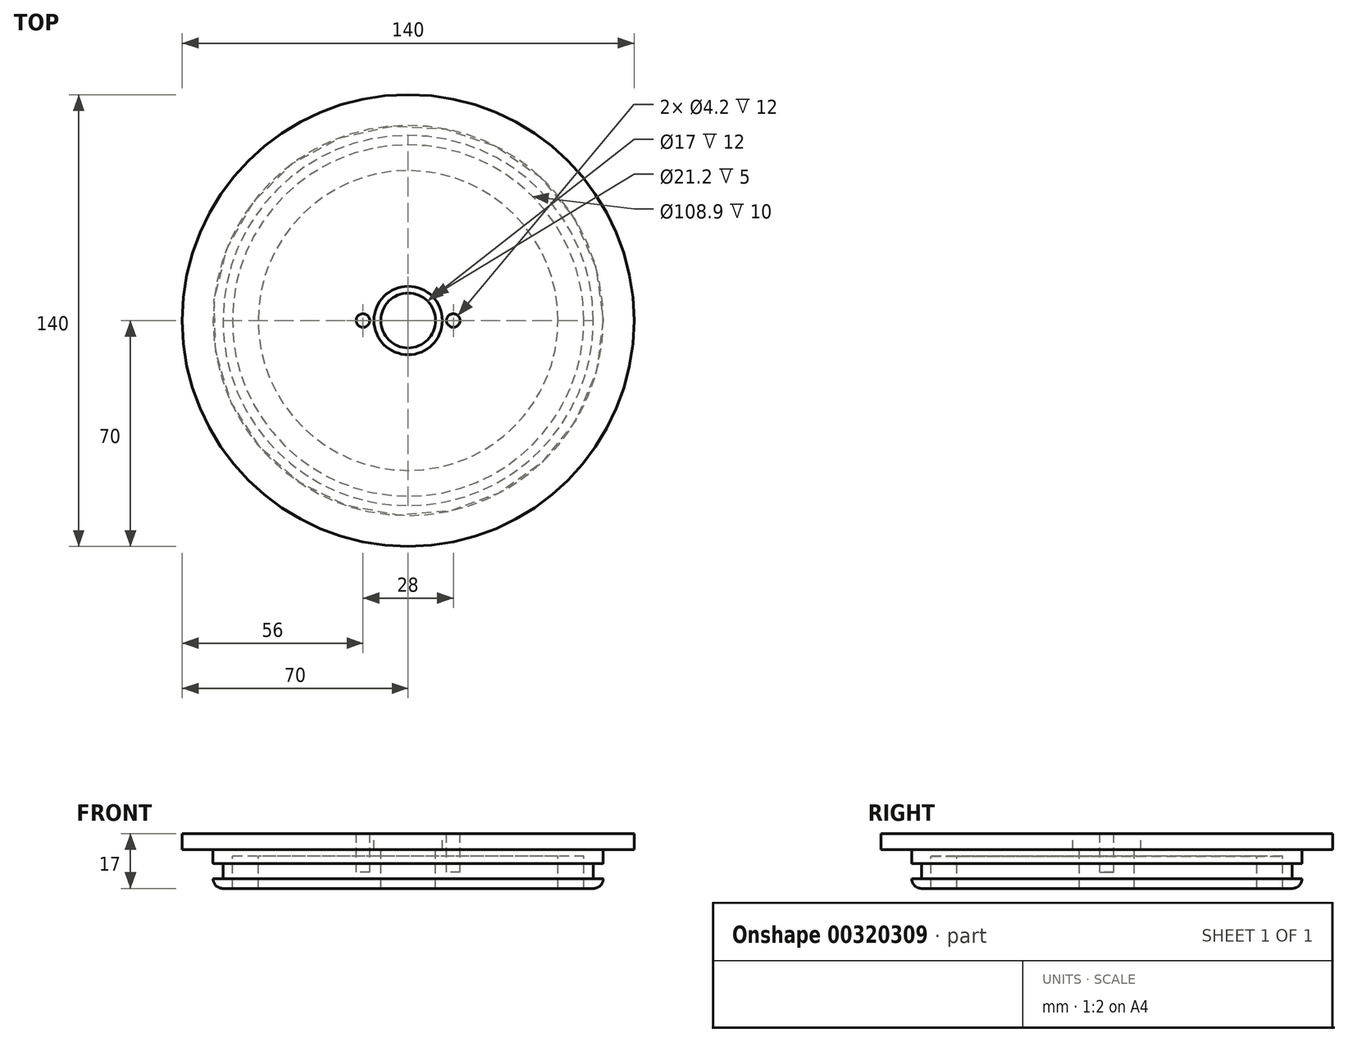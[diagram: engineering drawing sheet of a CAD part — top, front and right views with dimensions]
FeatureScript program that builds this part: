
annotation { "Feature Type Name" : "Feature", "Feature Type Description" : "" }
export const myFeature = defineFeature(function(context is Context, id is Id, definition is map)
    precondition{}
    {
        {
            var Q0;
            Q0=qCreatedBy(makeId("Front.planeOp"),FACE);
            var sketch = newSketch(context, id + "F0", { "sketchPlane" : qUnion([Q0])});
            skLineSegment(sketch, "E0", {"start": v(-10.6, 0) * mm, "end": v(-70, 0) * mm});
            skLineSegment(sketch, "E1", {"start": v(-70, 0) * mm, "end": v(-70, -5) * mm});
            skLineSegment(sketch, "E2", {"start": v(-70, -5) * mm, "end": v(-60.45, -5) * mm});
            skLineSegment(sketch, "E3", {"start": v(-60.45, -5) * mm, "end": v(-60.45, -9.15) * mm});
            skLineSegment(sketch, "E4", {"start": v(0, -17) * mm, "end": v(0, -5) * mm});
            skLineSegment(sketch, "E5", {"start": v(0, -17) * mm, "end": v(0, -14) * mm});
            skLineSegment(sketch, "E6", {"start": v(-57.38, -14) * mm, "end": v(-57.45, -14) * mm});
            skLineSegment(sketch, "E7", {"start": v(-57.38, -13.5) * mm, "end": v(-57.38, -9.8) * mm});
            skLineSegment(sketch, "E8", {"start": v(-57.88, -9.3) * mm, "end": v(-60.3, -9.3) * mm});
            skLineSegment(sketch, "E9", {"start": v(-57.88, -14) * mm, "end": v(-60.3, -14) * mm});
            skPoint(sketch, "E10.visualSharp", {"position": v(-60.45, -17) * mm});
            skLineSegment(sketch, "E11", {"start": v(-25, -11) * mm, "end": v(-25, -17) * mm});
            skPoint(sketch, "E11.endSnap0", {"position": v(-28.72, -17) * mm});
            skLineSegment(sketch, "E12", {"start": v(-25, -17) * mm, "end": v(-25, -7) * mm});
            skLineSegment(sketch, "E13", {"start": v(-25, -7) * mm, "end": v(-8.5, -7) * mm});
            skLineSegment(sketch, "E14", {"start": v(-10.6, -2.32) * mm, "end": v(-10.6, -5) * mm});
            skLineSegment(sketch, "E15", {"start": v(-10.6, -5) * mm, "end": v(-10.6, 0) * mm});
            skPoint(sketch, "E16.start.orphan", {"position": v(0, -2.32) * mm});
            skLineSegment(sketch, "E17", {"start": v(-10.6, -5) * mm, "end": v(-8.5, -5) * mm});
            skLineSegment(sketch, "E18", {"start": v(-8.5, -5) * mm, "end": v(-8.5, -7) * mm});
            skPoint(sketch, "E19.orphan", {"position": v(0, -7) * mm});
            skPoint(sketch, "E20.start.orphan", {"position": v(0, -11) * mm});
            skLineSegment(sketch, "E21", {"start": v(0, 0) * mm, "end": v(0, -17) * mm});
            skLineSegment(sketch, "E22", {"start": v(-60.45, -14) * mm, "end": v(-60.45, -14) * mm});
            skLineSegment(sketch, "E23", {"start": v(-25, -17) * mm, "end": v(-46.45, -17) * mm});
            skArc(sketch, "E24.filletArc", {"start": v(-60.45, -14.16) * mm, "mid": v(-59.51, -16.18) * mm, "end": v(-57.45, -17) * mm});
            skPoint(sketch, "E25.visualSharp", {"position": v(-60.45, -14) * mm});
            skArc(sketch, "E25.filletArc", {"start": v(-60.3, -14) * mm, "mid": v(-60.4, -14.05) * mm, "end": v(-60.45, -14.16) * mm});
            skPoint(sketch, "E26.visualSharp", {"position": v(-60.45, -9.3) * mm});
            skArc(sketch, "E26.filletArc", {"start": v(-60.45, -9.15) * mm, "mid": v(-60.4, -9.26) * mm, "end": v(-60.3, -9.3) * mm});
            skPoint(sketch, "E27.visualSharp", {"position": v(-57.38, -9.3) * mm});
            skArc(sketch, "E27.filletArc", {"start": v(-57.38, -9.8) * mm, "mid": v(-57.53, -9.45) * mm, "end": v(-57.88, -9.3) * mm});
            skPoint(sketch, "E28.visualSharp", {"position": v(-57.38, -14) * mm});
            skArc(sketch, "E28.filletArc", {"start": v(-57.88, -14) * mm, "mid": v(-57.53, -13.85) * mm, "end": v(-57.38, -13.5) * mm});
            skLineSegment(sketch, "E29", {"start": v(-8.5, -7) * mm, "end": v(-8.5, -17) * mm});
            skLineSegment(sketch, "E30", {"start": v(-8.5, -17) * mm, "end": v(-25, -17) * mm});
            skLineSegment(sketch, "E31.top", {"start": v(-54.45, -7) * mm, "end": v(-46.45, -7) * mm});
            skLineSegment(sketch, "E31.left", {"start": v(-54.45, -17) * mm, "end": v(-54.45, -7) * mm});
            skLineSegment(sketch, "E31.right", {"start": v(-46.45, -17) * mm, "end": v(-46.45, -7) * mm});
            skLineSegment(sketch, "E32.trimOffspring", {"start": v(-54.45, -17) * mm, "end": v(-57.45, -17) * mm});
            skSolve(sketch);
        }
        {
            var Q0;
            {var subQ1=sQuery(id+"F0.wireOp",EDGE,"E0");Q0=makeQuery(id+"F0.imprint","IMPRINT",FACE,{"disambiguationData":[TD([[makeQuery(id+"F0.imprint","IMPRINT",EDGE,{"derivedFrom":subQ1}),1.0]])]});}
            var Q1;
            {var subQ0=sQuery(id+"F0.wireOp",EDGE,"E13");Q1=makeQuery(id+"F0.imprint","IMPRINT",FACE,{"disambiguationData":[TD([[makeQuery(id+"F0.imprint","IMPRINT",EDGE,{"derivedFrom":subQ0}),-1.0]])]});}
            var Q2;
            Q2=sQuery(id+"F0.wireOp",EDGE,"E21");
            revolve(context, id + "F1", {"entities" : qUnion([Q0, Q1]), "axis" : qUnion([Q2]), "revolveType" : RevolveType.FULL, "surfaceOperationType" : NewSurfaceOperationType.NEW});
        }
        {
            var Q0;
            Q0=makeQuery(id+"F1.opRevolve","SWEPT_FACE",FACE,{"disambiguationData":[OSD([sQuery(id+"F0.wireOp",EDGE,"E0")])]});
            var sketch = newSketch(context, id + "F2", { "sketchPlane" : qUnion([Q0])});
            skCircle(sketch, "E33", {"center": v(0, 0) * mm, "radius": 14 * mm});
            skCircle(sketch, "E34", {"center": v(0, 14) * mm, "radius": 2 * mm});
            skCircle(sketch, "E35", {"center": v(0, -14) * mm, "radius": 2 * mm});
            skCircle(sketch, "E36", {"center": v(14, 0) * mm, "radius": 2.1 * mm});
            skCircle(sketch, "E37", {"center": v(-14, 0) * mm, "radius": 2.1 * mm});
            skSolve(sketch);
        }
        {
            var Q0;
            {var subQ0=sQuery(id+"F2.wireOp",EDGE,"E37");var subQ1=sQuery(id+"F2.wireOp",EDGE,"E33");var subQ2=makeQuery(id+"F2.imprint","INTERSECT",VERTEX,{"disambiguationData":[OD(0.0)],"derivedFrom":[subQ1,subQ0]});Q0=makeQuery(id+"F2.imprint","IMPRINT",FACE,{"disambiguationData":[TD([[makeQuery(id+"F2.imprint","IMPRINT",EDGE,{"disambiguationData":[TD([[subQ2,-1.0]])],"derivedFrom":subQ1}),1.0]])]});}
            var Q1;
            {var subQ0=sQuery(id+"F2.wireOp",EDGE,"E37");var subQ1=sQuery(id+"F2.wireOp",EDGE,"E33");var subQ2=makeQuery(id+"F2.imprint","INTERSECT",VERTEX,{"disambiguationData":[OD(0.0)],"derivedFrom":[subQ1,subQ0]});Q1=makeQuery(id+"F2.imprint","IMPRINT",FACE,{"disambiguationData":[TD([[makeQuery(id+"F2.imprint","IMPRINT",EDGE,{"disambiguationData":[TD([[subQ2,-1.0]])],"derivedFrom":subQ1}),-1.0]])]});}
            var Q2;
            {var subQ0=sQuery(id+"F2.wireOp",EDGE,"E36");var subQ1=sQuery(id+"F2.wireOp",EDGE,"E33");var subQ2=makeQuery(id+"F2.imprint","INTERSECT",VERTEX,{"disambiguationData":[OD(0.0)],"derivedFrom":[subQ1,subQ0]});Q2=makeQuery(id+"F2.imprint","IMPRINT",FACE,{"disambiguationData":[TD([[makeQuery(id+"F2.imprint","IMPRINT",EDGE,{"disambiguationData":[TD([[subQ2,1.0]])],"derivedFrom":subQ1}),1.0]])]});}
            var Q3;
            {var subQ0=sQuery(id+"F2.wireOp",EDGE,"E36");var subQ1=sQuery(id+"F2.wireOp",EDGE,"E33");var subQ2=makeQuery(id+"F2.imprint","INTERSECT",VERTEX,{"disambiguationData":[OD(0.0)],"derivedFrom":[subQ1,subQ0]});Q3=makeQuery(id+"F2.imprint","IMPRINT",FACE,{"disambiguationData":[TD([[makeQuery(id+"F2.imprint","IMPRINT",EDGE,{"disambiguationData":[TD([[subQ2,1.0]])],"derivedFrom":subQ1}),-1.0]])]});}
            extrude(context, id + "F3", {"entities" : qUnion([Q0, Q1, Q2, Q3]), "operationType" : NewBodyOperationType.REMOVE, "oppositeDirection" : true, "depth" : 12 * mm, "offsetDistance" : 25 * mm});
        }
    });
